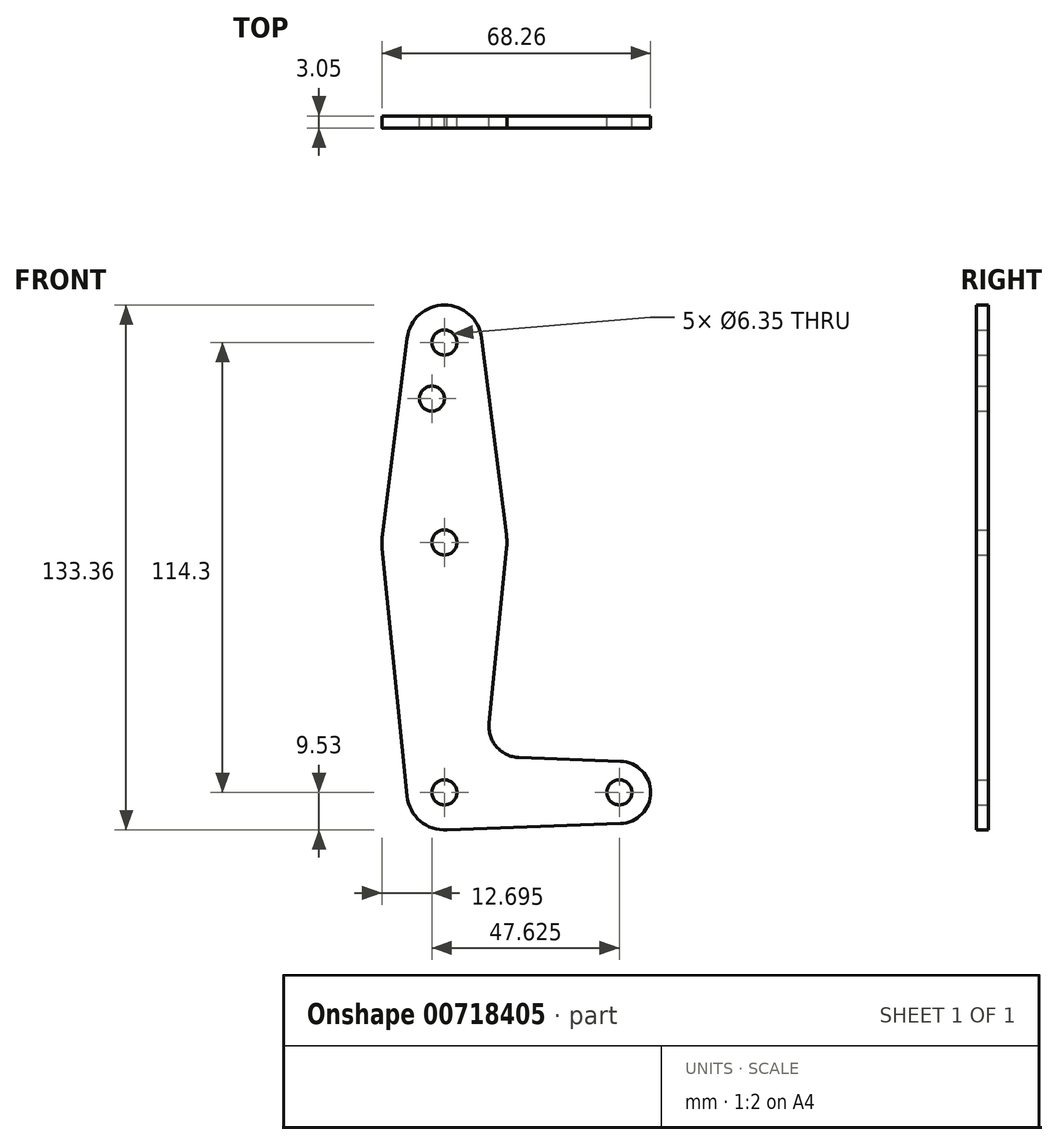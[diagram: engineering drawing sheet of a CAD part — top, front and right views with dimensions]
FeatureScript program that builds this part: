
annotation { "Feature Type Name" : "Feature", "Feature Type Description" : "" }
export const myFeature = defineFeature(function(context is Context, id is Id, definition is map)
    precondition{}
    {
        {
            var Q0;
            Q0=qCreatedBy(makeId("Front.planeOp"),FACE);
            var sketch = newSketch(context, id + "F0", { "sketchPlane" : qUnion([Q0])});
            skCircle(sketch, "E0", {"center": v(0, 0) * mm, "radius": 9.53 * mm});
            skLineSegment(sketch, "E1", {"start": v(0, 0) * mm, "end": v(44.45, 0) * mm, "construction": true});
            skCircle(sketch, "E2", {"center": v(44.45, 0) * mm, "radius": 7.94 * mm});
            skLineSegment(sketch, "E3", {"start": v(0, 0) * mm, "end": v(0, 114.3) * mm, "construction": true});
            skCircle(sketch, "E4", {"center": v(0, 114.3) * mm, "radius": 9.53 * mm});
            skCircle(sketch, "E5", {"center": v(0, 63.5) * mm, "radius": 15.88 * mm});
            skLineSegment(sketch, "E6", {"start": v(0, -9.53) * mm, "end": v(44.73, -7.93) * mm});
            skLineSegment(sketch, "E7", {"start": v(-15.75, 65.48) * mm, "end": v(-9.45, 115.5) * mm});
            skLineSegment(sketch, "E8", {"start": v(-9.48, -0.95) * mm, "end": v(-15.8, 61.91) * mm});
            skLineSegment(sketch, "E9", {"start": v(9.45, 115.5) * mm, "end": v(15.75, 65.48) * mm});
            skLineSegment(sketch, "E10", {"start": v(15.8, 61.91) * mm, "end": v(11.34, 17.6) * mm});
            skLineSegment(sketch, "E11", {"start": v(18.97, 8.85) * mm, "end": v(44.73, 7.93) * mm});
            skCircle(sketch, "E12", {"center": v(0, 114.3) * mm, "radius": 3.18 * mm});
            skCircle(sketch, "E13", {"center": v(0, 0) * mm, "radius": 3.18 * mm});
            skCircle(sketch, "E14", {"center": v(44.45, 0) * mm, "radius": 3.18 * mm});
            skCircle(sketch, "E15", {"center": v(0, 63.5) * mm, "radius": 3.18 * mm});
            skCircle(sketch, "E16", {"center": v(-3.18, 100.03) * mm, "radius": 3.18 * mm});
            skArc(sketch, "E17.filletArc", {"start": v(11.34, 17.6) * mm, "mid": v(13.26, 11.57) * mm, "end": v(18.97, 8.85) * mm});
            skSolve(sketch);
        }
        {
            var Q0;
            Q0 = qSketchRegion(id + "F0", true);
            extrude(context, id + "F1", {"entities" : qUnion([Q0]), "depth" : 3.05 * mm, "offsetDistance" : 25.4 * mm});
        }
    });
